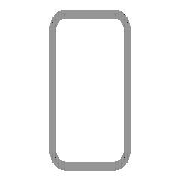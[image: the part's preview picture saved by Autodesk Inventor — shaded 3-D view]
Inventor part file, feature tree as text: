
AUTODESK INVENTOR PART (.ipt)
format: ipt  version: 2025.3 (Build 293356030, 356C)  size: 134,144 bytes
history: native  units: mm (DEFAULTED — no unit token found)
features: other x4, sketch x1, plane x1
ambient origin geometry x8: Origin, YZ Plane, XZ Plane, XY Plane, X Axis, Y Axis, Z Axis, Center Point
bodies: Solid1 (feature_tree), Body (feature_tree)
feature tree (6):
  parser-record x1  (decoder bookkeeping rows leaked as tree rows — omitted from the tree; the rows remain in map.json)
  other  "Driven Length"
  other  "Start Plane"
  other  "End Plane"
  sketch  "Sketch3"  dims[d3=340.0mm d4=0.0mm d7=4.0mm d9=20.0mm d11=40.0mm d12=2.0mm d13=40.0mm d14=380.0mm d15=10.0mm d16=20.0mm d17=90.0deg d18=340.0mm]
  plane  "Work Plane3"
